# Revit family: M_Floor Lamp - Arm Extension
name_source: partatom
category: Lighting Fixtures
revit_build: Autodesk Revit 2017 (Build: 20160109_1515(x64)
units: mm (PartAtom-declared; Revit-internal decimal feet)

## family parameters
Always vertical = Yes
Cut with Voids When Loaded = No
Light Source = Yes
OmniClass Number = 23.80.70.11.11
OmniClass Title = General Luminaries, Non Directional
Part Type = Normal
Room Calculation Point = No
Round Connector Dimension = Use Diameter
Shared = No
Work Plane-Based = No

## types (4) — shared parameters
Assembly Code = D5020230
Ballast Number of Poles = 1
Color Filter = 16777215
Dimming Lamp Color Temperature Shift = <None>
Lamp = T-4
Load Classification = Lighting - Dwelling Unit
Shade = Steel, Chrome Plated
Spot Beam Angle = 30.00°
Spot Field Angle = 90.00°
Stand = Steel, Chrome Plated
Tilt Angle = 90.00°

## per-type parameters (varying)
| type | Apparent Load | Ballast Voltage | Light Source Symbol Length | Wattage Comments |
| 100W - 120V | 100 VA | 120 V | 1000 mm  [stored 3.28084 ft] | 100 |
| 100W - 277V | 100 VA | 277 V | 3048 mm  [stored 10 ft] | 100 |
| 150W - 120V | 150 VA | 120 V | 3048 mm  [stored 10 ft] | 150 |
| 150W - 277V | 150 VA | 277 V | 3048 mm  [stored 10 ft] | 150 |

note: [stored X ft] marks values corroborated as IEEE doubles in the binary element streams (Revit-internal decimal feet)

## geometry (parser evidence)
native form markers: Blend x2, Sweep x1
no freeform markers — native parametric forms only
